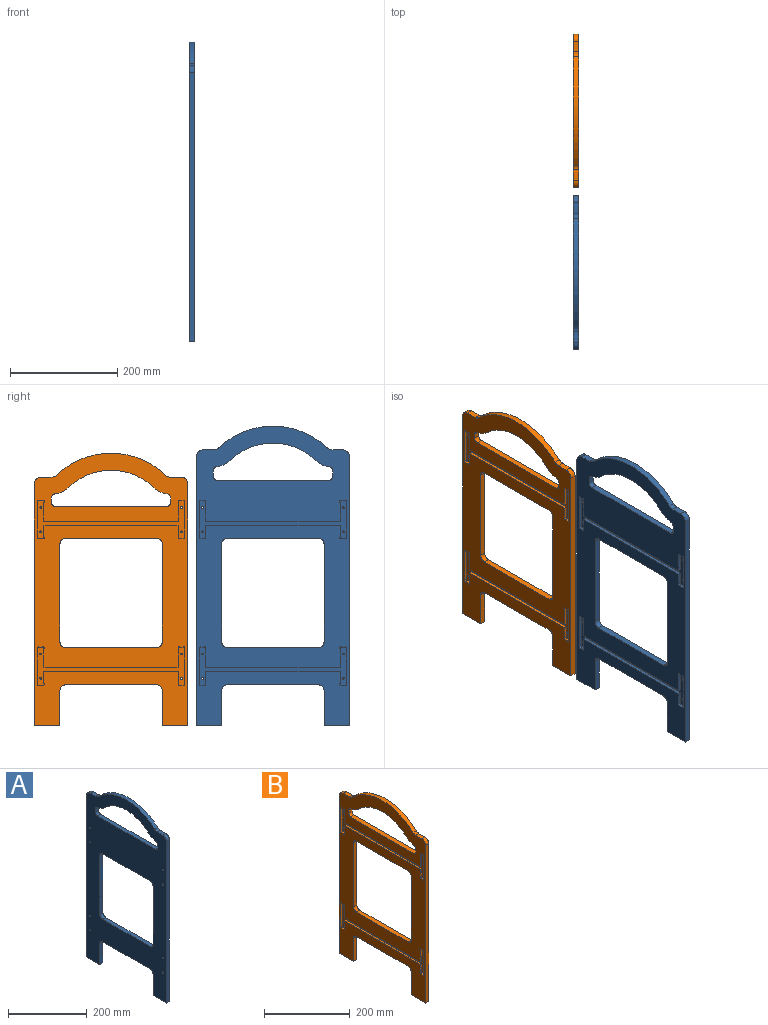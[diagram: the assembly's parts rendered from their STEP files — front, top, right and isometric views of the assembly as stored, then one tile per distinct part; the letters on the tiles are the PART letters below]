
ASSEMBLY  parts=2 mates=1
PART A: 86 faces, bbox 10.8x285.8x558.8 mm
  f0: cylinder r=7.62mm len=10.8mm, axis (1,0,0), area 118.9mm2, adj f1,f12,f18,f19
  f1: cylinder r=44.45mm len=25.3mm, axis (1,0,0), area 308.2mm2, adj f0,f2,f18,f19
  f2: cylinder r=113.96mm len=158.31mm, axis (1,0,0), area 1889.2mm2, adj f1,f3,f18,f19
  f3: cylinder r=44.45mm len=25.3mm, axis (1,0,0), area 308.2mm2, adj f2,f4,f18,f19
  f4: cylinder r=7.62mm len=10.8mm, axis (1,0,0), area 118.9mm2, adj f3,f13,f18,f19
  f5: plane 20.14x10.8mm, normal (0,0,1), area 217.5mm2, adj f6,f10,f18,f19
  f6: cylinder r=12.7mm len=10.8mm, axis (-1,0,0), area 105.3mm2, adj f5,f7,f18,f19
  f7: cylinder r=145.71mm len=202.42mm, axis (-1,0,0), area 2415.6mm2, adj f6,f8,f18,f19
  f8: cylinder r=12.7mm len=10.8mm, axis (-1,0,0), area 105.3mm2, adj f7,f9,f18,f19
  f9: plane 20.14x10.8mm, normal (0,0,1), area 217.5mm2, adj f8,f11,f18,f19
  f10: cylinder r=12.7mm len=12.7mm, axis (1,0,0), area 215.4mm2, adj f5,f16,f18,f19
  f11: cylinder r=12.7mm len=12.7mm, axis (1,0,0), area 215.4mm2, adj f9,f17,f18,f19
  f12: plane 10.8x10.57mm, normal (0,-1,0), area 114.1mm2, adj f0,f14,f18,f19
  f13: plane 10.8x10.57mm, normal (0,1,0), area 114.1mm2, adj f4,f15,f18,f19
  f14: cylinder r=7.62mm len=10.8mm, axis (-1,0,0), area 129.2mm2, adj f12,f18,f19,f20
  f15: cylinder r=7.62mm len=10.8mm, axis (-1,0,0), area 129.2mm2, adj f13,f18,f19,f20
  f16: plane 501.65x10.8mm, normal (0,-1,0), area 5415.3mm2, adj f10,f18,f19,f65
  f17: plane 501.65x10.8mm, normal (0,1,0), area 5415.3mm2, adj f11,f18,f19,f61
  f18: plane 558.8x285.75mm, normal (1,0,0), area 82087.6mm2, adj f0,f1,f2,f3,f4,f5,f6,f7
  f19: plane 558.8x285.75mm, normal (-1,0,0), area 88882.4mm2, adj f0,f1,f2,f3,f4,f5,f6,f7
  f20: plane 207.01x10.8mm, normal (0,0,1), area 2234.7mm2, adj f14,f15,f18,f19
  f21: plane 6.17x5.4mm, normal (0,0,1), area 33.3mm2, adj f18,f59,f60,f76
  f22: plane 65.22x5.4mm, normal (0,-1,0), area 352mm2, adj f18,f57,f60,f76
  f23: plane 22.71x5.4mm, normal (0,1,0), area 122.6mm2, adj f18,f42,f59,f76
  f24: plane 6.17x5.4mm, normal (0,0,-1), area 33.3mm2, adj f18,f57,f58,f76
  f25: plane 35.41x5.4mm, normal (0,1,0), area 191.1mm2, adj f18,f41,f58,f76
  f26: plane 6.17x5.4mm, normal (0,0,-1), area 33.3mm2, adj f18,f55,f56,f76
  f27: plane 65.22x5.4mm, normal (0,1,0), area 352mm2, adj f18,f54,f56,f76
  f28: plane 35.41x5.4mm, normal (0,-1,0), area 191.1mm2, adj f18,f41,f55,f76
  f29: plane 6.17x5.4mm, normal (0,0,1), area 33.3mm2, adj f18,f53,f54,f76
  f30: plane 22.71x5.4mm, normal (0,-1,0), area 122.6mm2, adj f18,f42,f53,f76
  f31: plane 6.17x5.4mm, normal (0,0,-1), area 33.3mm2, adj f18,f51,f52,f77
  f32: plane 35.41x5.4mm, normal (0,1,0), area 191.1mm2, adj f18,f43,f52,f77
  f33: plane 65.22x5.4mm, normal (0,-1,0), area 352mm2, adj f18,f49,f51,f77
  f34: plane 6.17x5.4mm, normal (0,0,1), area 33.3mm2, adj f18,f49,f50,f77
  f35: plane 22.71x5.4mm, normal (0,1,0), area 122.6mm2, adj f18,f44,f50,f77
  f36: plane 6.17x5.4mm, normal (0,0,1), area 33.3mm2, adj f18,f47,f48,f77
  f37: plane 22.71x5.4mm, normal (0,-1,0), area 122.6mm2, adj f18,f44,f48,f77
  f38: plane 65.22x5.4mm, normal (0,1,0), area 352mm2, adj f18,f45,f47,f77
  f39: plane 6.17x5.4mm, normal (0,0,-1), area 33.3mm2, adj f18,f45,f46,f77
  f40: plane 35.41x5.4mm, normal (0,-1,0), area 191.1mm2, adj f18,f43,f46,f77
  f41: plane 250.7x5.4mm, normal (0,0,-1), area 1353.1mm2, adj f18,f25,f28,f76
  f42: plane 250.7x5.4mm, normal (0,0,1), area 1353.1mm2, adj f18,f23,f30,f76
  f43: plane 250.7x5.4mm, normal (0,0,-1), area 1353.1mm2, adj f18,f32,f40,f77
  f44: plane 250.7x5.4mm, normal (0,0,1), area 1353.1mm2, adj f18,f35,f37,f77
  f45: cylinder r=1.91mm len=5.4mm, axis (1,0,0), area 32.3mm2, adj f18,f38,f39,f77
  f46: cylinder r=1.91mm len=5.4mm, axis (1,0,0), area 32.3mm2, adj f18,f39,f40,f77
  f47: cylinder r=1.91mm len=5.4mm, axis (1,0,0), area 32.3mm2, adj f18,f36,f38,f77
  f48: cylinder r=1.91mm len=5.4mm, axis (1,0,0), area 32.3mm2, adj f18,f36,f37,f77
  f49: cylinder r=1.91mm len=5.4mm, axis (1,0,0), area 32.3mm2, adj f18,f33,f34,f77
  f50: cylinder r=1.91mm len=5.4mm, axis (1,0,0), area 32.3mm2, adj f18,f34,f35,f77
  f51: cylinder r=1.91mm len=5.4mm, axis (1,0,0), area 32.3mm2, adj f18,f31,f33,f77
  f52: cylinder r=1.91mm len=5.4mm, axis (1,0,0), area 32.3mm2, adj f18,f31,f32,f77
  f53: cylinder r=1.91mm len=5.4mm, axis (1,0,0), area 32.3mm2, adj f18,f29,f30,f76
  f54: cylinder r=1.91mm len=5.4mm, axis (1,0,0), area 32.3mm2, adj f18,f27,f29,f76
  f55: cylinder r=1.91mm len=5.4mm, axis (1,0,0), area 32.3mm2, adj f18,f26,f28,f76
  f56: cylinder r=1.91mm len=5.4mm, axis (1,0,0), area 32.3mm2, adj f18,f26,f27,f76
  f57: cylinder r=1.91mm len=5.4mm, axis (1,0,0), area 32.3mm2, adj f18,f22,f24,f76
  f58: cylinder r=1.91mm len=5.4mm, axis (1,0,0), area 32.3mm2, adj f18,f24,f25,f76
  f59: cylinder r=1.91mm len=5.4mm, axis (1,0,0), area 32.3mm2, adj f18,f21,f23,f76
  f60: cylinder r=1.91mm len=5.4mm, axis (1,0,0), area 32.3mm2, adj f18,f21,f22,f76
  f61: plane 47.63x10.8mm, normal (0,0,-1), area 514.1mm2, adj f17,f18,f19,f62
  f62: plane 66.04x10.8mm, normal (0,-1,0), area 712.9mm2, adj f18,f19,f61,f75
  f63: plane 170.18x10.8mm, normal (0,0,-1), area 1837.1mm2, adj f18,f19,f74,f75
  f64: plane 66.04x10.8mm, normal (0,1,0), area 712.9mm2, adj f18,f19,f65,f74
  f65: plane 47.63x10.8mm, normal (0,0,-1), area 514.1mm2, adj f16,f18,f19,f64
  f66: plane 182.88x10.8mm, normal (0,1,0), area 1974.2mm2, adj f18,f19,f70,f71
  f67: plane 170.18x10.8mm, normal (0,0,1), area 1837.1mm2, adj f18,f19,f71,f73
  f68: plane 182.88x10.8mm, normal (0,-1,0), area 1974.2mm2, adj f18,f19,f72,f73
  f69: plane 170.18x10.8mm, normal (0,0,-1), area 1837.1mm2, adj f18,f19,f70,f72
  f70: cylinder r=10.16mm len=10.8mm, axis (1,0,0), area 172.3mm2, adj f18,f19,f66,f69
  f71: cylinder r=10.16mm len=10.8mm, axis (-1,0,0), area 172.3mm2, adj f18,f19,f66,f67
  f72: cylinder r=10.16mm len=10.8mm, axis (-1,0,0), area 172.3mm2, adj f18,f19,f68,f69
  f73: cylinder r=10.16mm len=10.8mm, axis (1,0,0), area 172.3mm2, adj f18,f19,f67,f68
  f74: cylinder r=10.16mm len=10.8mm, axis (-1,0,0), area 172.3mm2, adj f18,f19,f63,f64
  f75: cylinder r=10.16mm len=10.8mm, axis (1,0,0), area 172.3mm2, adj f18,f19,f62,f63
  f76: plane 274.93x71.73mm, normal (1,0,0), area 3397.4mm2, adj f21,f22,f23,f24,f25,f26,f27,f28
  f77: plane 274.93x71.73mm, normal (1,0,0), area 3397.4mm2, adj f31,f32,f33,f34,f35,f36,f37,f38
  f78: cylinder r=1.65mm len=5.4mm, axis (1,0,0), area 56mm2, adj f19,f77
  f79: cylinder r=1.65mm len=5.4mm, axis (1,0,0), area 56mm2, adj f19,f77
  f80: cylinder r=1.65mm len=5.4mm, axis (1,0,0), area 56mm2, adj f19,f77
  f81: cylinder r=1.65mm len=5.4mm, axis (1,0,0), area 56mm2, adj f19,f77
  f82: cylinder r=1.65mm len=5.4mm, axis (1,0,0), area 56mm2, adj f19,f76
  f83: cylinder r=1.65mm len=5.4mm, axis (1,0,0), area 56mm2, adj f19,f76
  f84: cylinder r=1.65mm len=5.4mm, axis (1,0,0), area 56mm2, adj f19,f76
  f85: cylinder r=1.65mm len=5.4mm, axis (1,0,0), area 56mm2, adj f19,f76
PART B: 86 faces, bbox 10.8x285.8x508.2 mm
  f0: cylinder r=7.62mm len=10.8mm, axis (1,0,0), area 118.9mm2, adj f1,f12,f16,f17
  f1: cylinder r=44.45mm len=25.3mm, axis (1,0,0), area 308.2mm2, adj f0,f2,f16,f17
  f2: cylinder r=113.96mm len=158.31mm, axis (1,0,0), area 1889.2mm2, adj f1,f3,f16,f17
  f3: cylinder r=44.45mm len=25.3mm, axis (1,0,0), area 308.2mm2, adj f2,f4,f16,f17
  f4: cylinder r=7.62mm len=10.8mm, axis (1,0,0), area 118.9mm2, adj f3,f13,f16,f17
  f5: plane 20.14x10.8mm, normal (0,0,1), area 217.5mm2, adj f6,f10,f16,f17
  f6: cylinder r=12.7mm len=10.8mm, axis (-1,0,0), area 105.3mm2, adj f5,f7,f16,f17
  f7: cylinder r=145.71mm len=202.42mm, axis (-1,0,0), area 2415.6mm2, adj f6,f8,f16,f17
  f8: cylinder r=12.7mm len=10.8mm, axis (-1,0,0), area 105.3mm2, adj f7,f9,f16,f17
  f9: plane 20.14x10.8mm, normal (0,0,1), area 217.5mm2, adj f8,f11,f16,f17
  f10: cylinder r=12.7mm len=12.7mm, axis (1,0,0), area 215.4mm2, adj f5,f14,f16,f17
  f11: cylinder r=12.7mm len=12.7mm, axis (1,0,0), area 215.4mm2, adj f9,f15,f16,f17
  f12: plane 10.8x8.44mm, normal (0,-1,0), area 91.1mm2, adj f0,f16,f17,f85
  f13: plane 10.8x8.44mm, normal (0,1,0), area 91.1mm2, adj f4,f16,f17,f83
  f14: plane 451.03x10.8mm, normal (0,-1,0), area 4868.8mm2, adj f10,f16,f17,f58
  f15: plane 451.03x10.8mm, normal (0,1,0), area 4868.8mm2, adj f11,f16,f17,f59
  f16: plane 508.18x285.75mm, normal (1,0,0), area 74902.7mm2, adj f0,f1,f2,f3,f4,f5,f6,f7
  f17: plane 508.18x285.75mm, normal (-1,0,0), area 68107.9mm2, adj f0,f1,f2,f3,f4,f5,f6,f7
  f18: plane 250.7x5.4mm, normal (0,0,-1), area 1353.1mm2, adj f17,f19,f20,f73
  f19: plane 35.41x5.4mm, normal (0,1,0), area 191.1mm2, adj f17,f18,f55,f73
  f20: plane 35.41x5.4mm, normal (0,-1,0), area 191.1mm2, adj f17,f18,f47,f73
  f21: plane 250.7x5.4mm, normal (0,0,1), area 1353.1mm2, adj f17,f22,f23,f74
  f22: plane 22.71x5.4mm, normal (0,1,0), area 122.6mm2, adj f17,f21,f53,f74
  f23: plane 22.71x5.4mm, normal (0,-1,0), area 122.6mm2, adj f17,f21,f45,f74
  f24: plane 250.7x5.4mm, normal (0,0,-1), area 1353.1mm2, adj f17,f25,f26,f74
  f25: plane 35.41x5.4mm, normal (0,1,0), area 191.1mm2, adj f17,f24,f51,f74
  f26: plane 35.41x5.4mm, normal (0,-1,0), area 191.1mm2, adj f17,f24,f43,f74
  f27: plane 250.7x5.4mm, normal (0,0,1), area 1353.1mm2, adj f17,f28,f29,f73
  f28: plane 22.71x5.4mm, normal (0,1,0), area 122.6mm2, adj f17,f27,f57,f73
  f29: plane 22.71x5.4mm, normal (0,-1,0), area 122.6mm2, adj f17,f27,f49,f73
  f30: plane 6.17x5.4mm, normal (0,0,1), area 33.3mm2, adj f17,f56,f57,f73
  f31: plane 65.22x5.4mm, normal (0,-1,0), area 352mm2, adj f17,f54,f56,f73
  f32: plane 6.17x5.4mm, normal (0,0,-1), area 33.3mm2, adj f17,f54,f55,f73
  f33: plane 6.17x5.4mm, normal (0,0,1), area 33.3mm2, adj f17,f52,f53,f74
  f34: plane 65.22x5.4mm, normal (0,-1,0), area 352mm2, adj f17,f50,f52,f74
  f35: plane 6.17x5.4mm, normal (0,0,-1), area 33.3mm2, adj f17,f50,f51,f74
  f36: plane 6.17x5.4mm, normal (0,0,1), area 33.3mm2, adj f17,f48,f49,f73
  f37: plane 65.22x5.4mm, normal (0,1,0), area 352mm2, adj f17,f46,f48,f73
  f38: plane 6.17x5.4mm, normal (0,0,-1), area 33.3mm2, adj f17,f46,f47,f73
  f39: plane 6.17x5.4mm, normal (0,0,1), area 33.3mm2, adj f17,f44,f45,f74
  f40: plane 65.22x5.4mm, normal (0,1,0), area 352mm2, adj f17,f42,f44,f74
  f41: plane 6.17x5.4mm, normal (0,0,-1), area 33.3mm2, adj f17,f42,f43,f74
  f42: cylinder r=1.91mm len=5.4mm, axis (-1,0,0), area 32.3mm2, adj f17,f40,f41,f74
  f43: cylinder r=1.91mm len=5.4mm, axis (-1,0,0), area 32.3mm2, adj f17,f26,f41,f74
  f44: cylinder r=1.91mm len=5.4mm, axis (-1,0,0), area 32.3mm2, adj f17,f39,f40,f74
  f45: cylinder r=1.91mm len=5.4mm, axis (-1,0,0), area 32.3mm2, adj f17,f23,f39,f74
  f46: cylinder r=1.91mm len=5.4mm, axis (-1,0,0), area 32.3mm2, adj f17,f37,f38,f73
  f47: cylinder r=1.91mm len=5.4mm, axis (-1,0,0), area 32.3mm2, adj f17,f20,f38,f73
  f48: cylinder r=1.91mm len=5.4mm, axis (-1,0,0), area 32.3mm2, adj f17,f36,f37,f73
  f49: cylinder r=1.91mm len=5.4mm, axis (-1,0,0), area 32.3mm2, adj f17,f29,f36,f73
  f50: cylinder r=1.91mm len=5.4mm, axis (-1,0,0), area 32.3mm2, adj f17,f34,f35,f74
  f51: cylinder r=1.91mm len=5.4mm, axis (-1,0,0), area 32.3mm2, adj f17,f25,f35,f74
  f52: cylinder r=1.91mm len=5.4mm, axis (-1,0,0), area 32.3mm2, adj f17,f33,f34,f74
  f53: cylinder r=1.91mm len=5.4mm, axis (-1,0,0), area 32.3mm2, adj f17,f22,f33,f74
  f54: cylinder r=1.91mm len=5.4mm, axis (-1,0,0), area 32.3mm2, adj f17,f31,f32,f73
  f55: cylinder r=1.91mm len=5.4mm, axis (-1,0,0), area 32.3mm2, adj f17,f19,f32,f73
  f56: cylinder r=1.91mm len=5.4mm, axis (-1,0,0), area 32.3mm2, adj f17,f30,f31,f73
  f57: cylinder r=1.91mm len=5.4mm, axis (-1,0,0), area 32.3mm2, adj f17,f28,f30,f73
  f58: plane 47.63x10.8mm, normal (0,0,-1), area 514.1mm2, adj f14,f16,f17,f62
  f59: plane 47.63x10.8mm, normal (0,0,-1), area 514.1mm2, adj f15,f16,f17,f61
  f60: plane 170.18x10.8mm, normal (0,0,-1), area 1837.1mm2, adj f16,f17,f71,f72
  f61: plane 66.04x10.8mm, normal (0,-1,0), area 712.9mm2, adj f16,f17,f59,f71
  f62: plane 66.04x10.8mm, normal (0,1,0), area 712.9mm2, adj f16,f17,f58,f72
  f63: plane 182.88x10.8mm, normal (0,-1,0), area 1974.2mm2, adj f16,f17,f69,f70
  f64: plane 170.18x10.8mm, normal (0,0,1), area 1837.1mm2, adj f16,f17,f68,f69
  f65: plane 182.88x10.8mm, normal (0,1,0), area 1974.2mm2, adj f16,f17,f67,f68
  f66: plane 170.18x10.8mm, normal (0,0,-1), area 1837.1mm2, adj f16,f17,f67,f70
  f67: cylinder r=10.16mm len=10.8mm, axis (1,0,0), area 172.3mm2, adj f16,f17,f65,f66
  f68: cylinder r=10.16mm len=10.8mm, axis (-1,0,0), area 172.3mm2, adj f16,f17,f64,f65
  f69: cylinder r=10.16mm len=10.8mm, axis (1,0,0), area 172.3mm2, adj f16,f17,f63,f64
  f70: cylinder r=10.16mm len=10.8mm, axis (-1,0,0), area 172.3mm2, adj f16,f17,f63,f66
  f71: cylinder r=10.16mm len=10.8mm, axis (1,0,0), area 172.3mm2, adj f16,f17,f60,f61
  f72: cylinder r=10.16mm len=10.8mm, axis (-1,0,0), area 172.3mm2, adj f16,f17,f60,f62
  f73: plane 274.93x71.73mm, normal (-1,0,0), area 3397.4mm2, adj f18,f19,f20,f27,f28,f29,f30,f31
  f74: plane 274.93x71.73mm, normal (-1,0,0), area 3397.4mm2, adj f21,f22,f23,f24,f25,f26,f33,f34
  f75: cylinder r=1.65mm len=5.4mm, axis (1,0,0), area 56mm2, adj f16,f74
  f76: cylinder r=1.65mm len=5.4mm, axis (1,0,0), area 56mm2, adj f16,f74
  f77: cylinder r=1.65mm len=5.4mm, axis (1,0,0), area 56mm2, adj f16,f74
  f78: cylinder r=1.65mm len=5.4mm, axis (1,0,0), area 56mm2, adj f16,f74
  f79: cylinder r=1.65mm len=5.4mm, axis (1,0,0), area 56mm2, adj f16,f73
  f80: cylinder r=1.65mm len=5.4mm, axis (1,0,0), area 56mm2, adj f16,f73
  f81: cylinder r=1.65mm len=5.4mm, axis (1,0,0), area 56mm2, adj f16,f73
  f82: cylinder r=1.65mm len=5.4mm, axis (1,0,0), area 56mm2, adj f16,f73
  f83: cylinder r=7.62mm len=10.8mm, axis (1,0,0), area 118.9mm2, adj f13,f16,f17,f84
  f84: plane 208.92x10.8mm, normal (0,0,1), area 2255.3mm2, adj f16,f17,f83,f85
  f85: cylinder r=7.62mm len=10.8mm, axis (1,0,0), area 118.9mm2, adj f12,f16,f17,f84
PLACE A rot(axis=(0,0,1),180deg) t=(-473.92,-367.7,302.64)mm
PLACE B t=(-473.92,219.67,302.64)mm fixed
MATE fastened B.f17 <-> A.f18  axis (-1,0,0) through (-192.61,-66.08,23.24)mm
